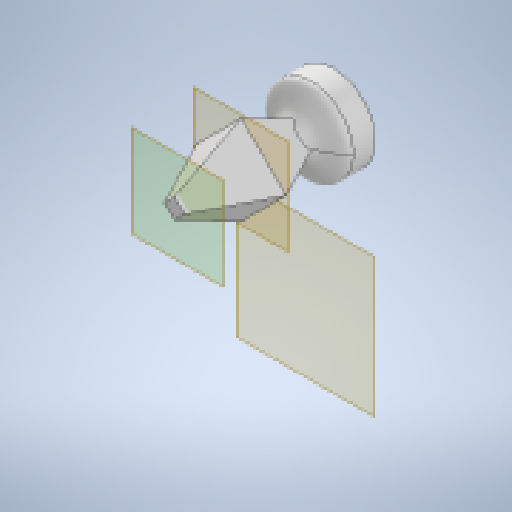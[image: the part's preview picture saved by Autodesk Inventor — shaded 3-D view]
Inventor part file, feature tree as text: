
AUTODESK INVENTOR PART (.ipt)
format: ipt  version: 2024.1 (Build 281209000, 209)  size: 232,448 bytes
history: native  units: in
note: dims shown in document units (in); Inventor stores cm internally (conversion verified against a paired STEP export)
features: other x5, sketch x5, extrude x4, plane x3, revolve x1, projected_geometry x1
ambient origin geometry x8: Origin, YZ Plane, XZ Plane, XY Plane, X Axis, Y Axis, Z Axis, Center Point
bodies: Body1 (feature_tree)
feature tree (19):
  other  "pawn-white"
  extrude  "Extrusion1"  Depth=0.5906in
  extrude  "Extrusion2"  Depth=0.0354in TaperAngle=0.0deg
  other  "Work Axis1"
  revolve  "Revolution1"  Angle=90.0deg
  plane  "Work Plane3"
  extrude  "Extrusion3"  Depth=0.315in
  extrude  "Extrusion4"  Depth=0.315in
  sketch  "Sketch1"  dims[d0=0.2362in d1=0.5906in]
  sketch  "Sketch2"  dims[d2=0.1575in d3=0.0in d4=0.0354in d5=0.0in]
  sketch  "Sketch3"  dims[d6=1.1024in d7=90.0deg]
  plane  "Work Plane1"
  plane  "Work Plane2"
  sketch  "Sketch4"  dims[d8=-1.1024in d9=0.315in]
  sketch  "Sketch5"  dims[d10=0.315in d11=0.315in d12=0.315in d13=0.4724in d14=-0.1374in d15=0.4724in d16=-0.1374in]
  projected_geometry  "Projected Loop1"
  other  "<userpath>\Documents\0004-CAD\3D-cad-main\chess-set\chess-set-one.iam"
  other  "chess-set-one.iam"
  other  "board:1"
